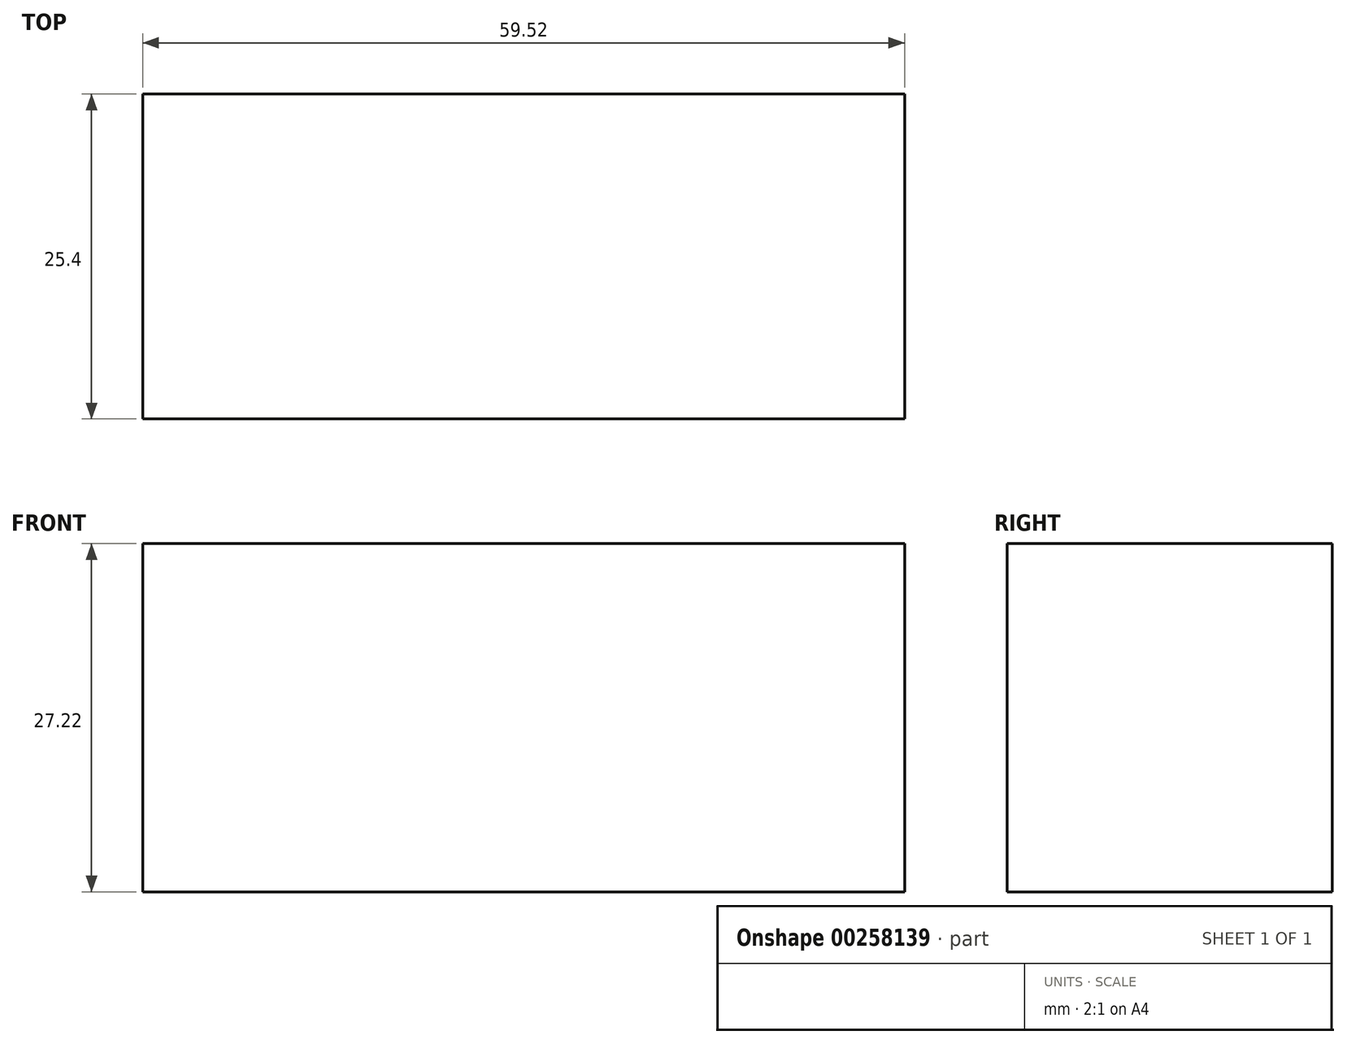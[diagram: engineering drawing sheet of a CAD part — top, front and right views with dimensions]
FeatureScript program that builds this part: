
annotation { "Feature Type Name" : "Feature", "Feature Type Description" : "" }
export const myFeature = defineFeature(function(context is Context, id is Id, definition is map)
    precondition{}
    {
        {
            var Q0;
            Q0=qCreatedBy(makeId("Front.planeOp"),FACE);
            var sketch = newSketch(context, id + "F0", { "sketchPlane" : qUnion([Q0])});
            skLineSegment(sketch, "E0.bottom", {"start": v(-29.33, -13.6) * mm, "end": v(30.2, -13.6) * mm});
            skLineSegment(sketch, "E0.top", {"start": v(-29.33, 13.6) * mm, "end": v(30.2, 13.6) * mm});
            skLineSegment(sketch, "E0.left", {"start": v(-29.33, -13.6) * mm, "end": v(-29.33, 13.6) * mm});
            skLineSegment(sketch, "E0.right", {"start": v(30.2, -13.6) * mm, "end": v(30.2, 13.6) * mm});
            skPoint(sketch, "E0.middle", {"position": v(0.43, 0) * mm});
            skSolve(sketch);
        }
        {
            var Q0;
            Q0=makeQuery(id+"F0.imprint","IMPRINT",FACE,{"disambiguationData":[TD([[makeQuery(id+"F0.imprint","IMPRINT",EDGE,{"derivedFrom":sQuery(id+"F0.wireOp",EDGE,"E0.bottom")}),1.0]])]});
            extrude(context, id + "F1", {"entities" : qUnion([Q0]), "depth" : 25.4 * mm});
        }
    });
